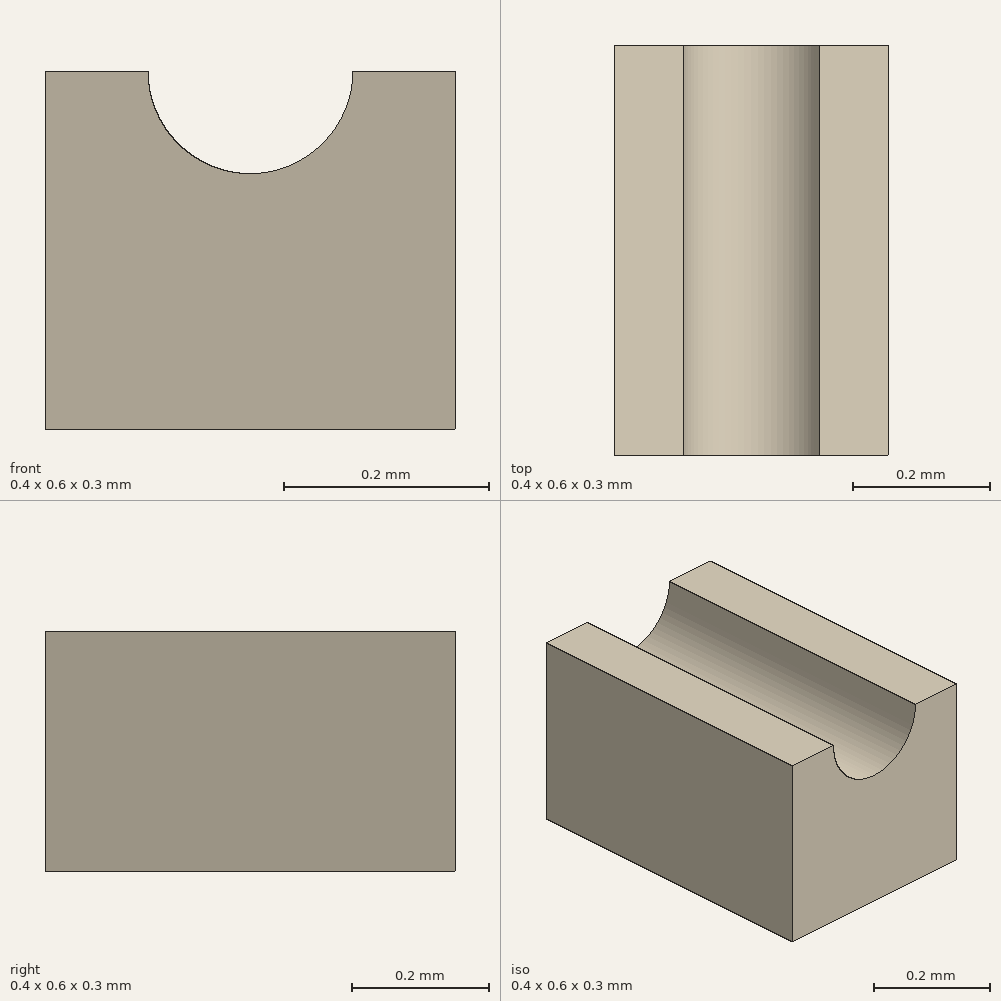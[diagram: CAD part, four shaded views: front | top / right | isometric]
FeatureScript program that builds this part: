
annotation { "Feature Type Name" : "Feature", "Feature Type Description" : "" }
export const myFeature = defineFeature(function(context is Context, id is Id, definition is map)
    precondition{}
    {
        {
            var Q0;
            Q0=qCreatedBy(makeId("Front.planeOp"),FACE);
            var sketch = newSketch(context, id + "F0", { "sketchPlane" : qUnion([Q0])});
            skLineSegment(sketch, "E0.bottom", {"start": v(0.2, 0.17) * mm, "end": v(0.1, 0.17) * mm});
            skLineSegment(sketch, "E0.top", {"start": v(0.2, -0.17) * mm, "end": v(-0.2, -0.17) * mm});
            skLineSegment(sketch, "E0.left", {"start": v(0.2, 0.18) * mm, "end": v(0.2, -0.17) * mm});
            skLineSegment(sketch, "E0.right", {"start": v(-0.2, 0.17) * mm, "end": v(-0.2, -0.18) * mm});
            skPoint(sketch, "E0.middle", {"position": v(0, 0) * mm});
            skArc(sketch, "E1", {"start": v(-0.1, 0.17) * mm, "mid": v(0, 0.07) * mm, "end": v(0.1, 0.17) * mm});
            skLineSegment(sketch, "E2.trimOffspring", {"start": v(-0.1, 0.17) * mm, "end": v(-0.2, 0.17) * mm});
            skSolve(sketch);
        }
        {
            var Q0;
            Q0=makeQuery(id+"F0.imprint","IMPRINT",FACE,{"disambiguationData":[TD([[makeQuery(id+"F0.imprint","IMPRINT",EDGE,{"derivedFrom":sQuery(id+"F0.wireOp",EDGE,"E0.bottom")}),1.0]])]});
            extrude(context, id + "F1", {"entities" : qUnion([Q0]), "depth" : 0.6 * mm});
        }
    });
